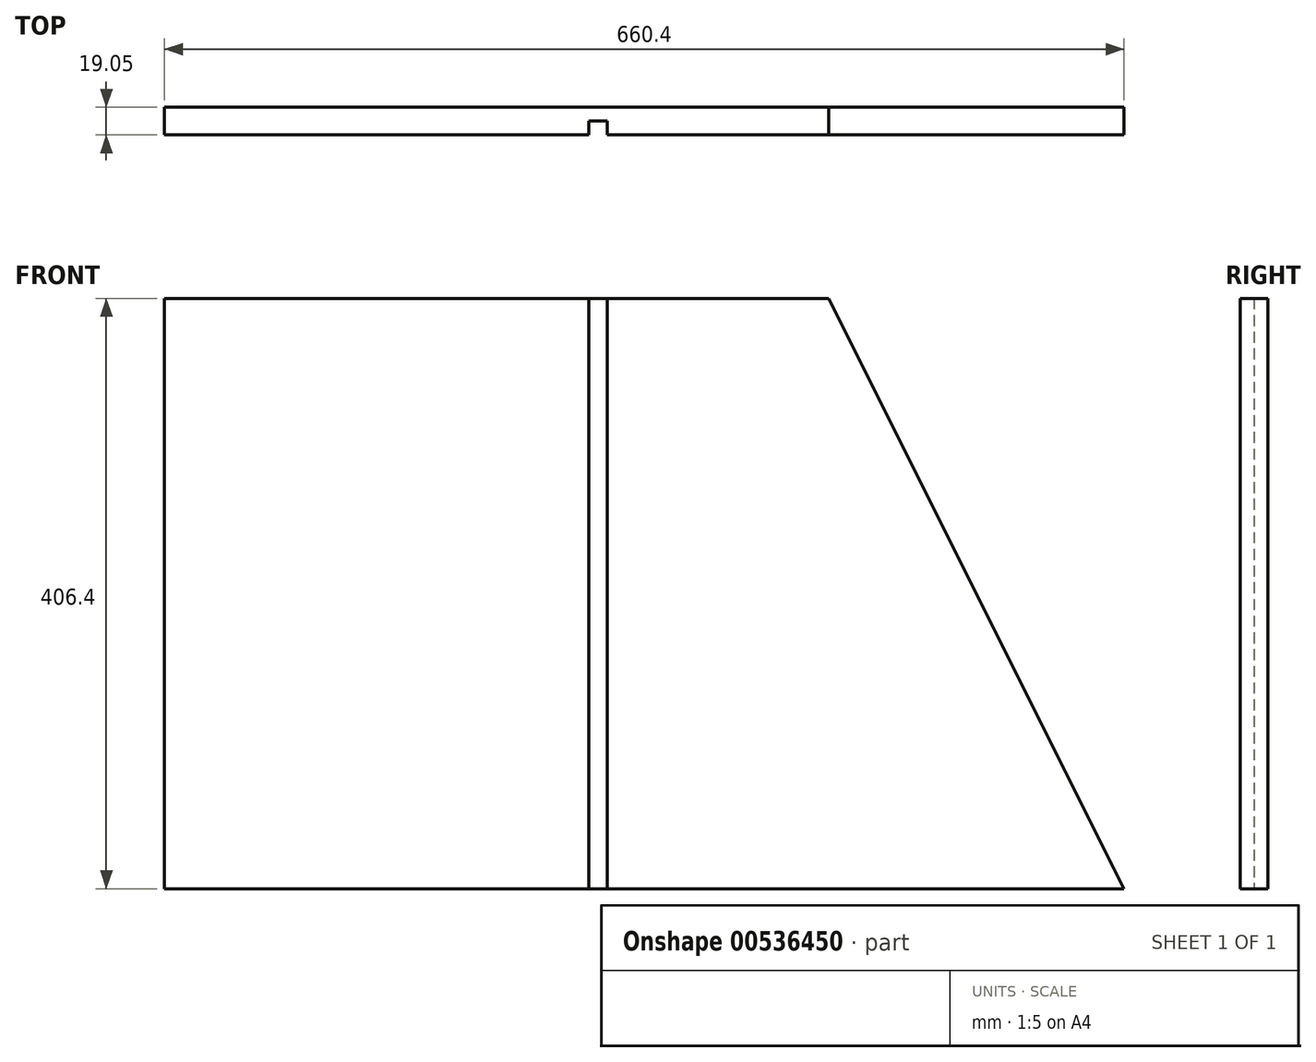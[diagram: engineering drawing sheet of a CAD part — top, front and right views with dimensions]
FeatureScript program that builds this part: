
annotation { "Feature Type Name" : "Feature", "Feature Type Description" : "" }
export const myFeature = defineFeature(function(context is Context, id is Id, definition is map)
    precondition{}
    {
        {
            var Q0;
            Q0=qCreatedBy(makeId("Front.planeOp"),FACE);
            var sketch = newSketch(context, id + "F0", { "sketchPlane" : qUnion([Q0])});
            skLineSegment(sketch, "E0", {"start": v(-356.65, 252.41) * mm, "end": v(-229.65, 252.41) * mm});
            skLineSegment(sketch, "E1", {"start": v(-229.65, 252.41) * mm, "end": v(-26.45, -153.99) * mm});
            skLineSegment(sketch, "E2", {"start": v(-26.45, -153.99) * mm, "end": v(-686.85, -153.99) * mm});
            skLineSegment(sketch, "E3", {"start": v(-229.65, 252.41) * mm, "end": v(-229.65, -153.99) * mm});
            skLineSegment(sketch, "E4.bottom", {"start": v(-356.65, 252.41) * mm, "end": v(-686.85, 252.41) * mm});
            skLineSegment(sketch, "E4.top", {"start": v(-356.65, -153.99) * mm, "end": v(-686.85, -153.99) * mm});
            skLineSegment(sketch, "E4.right", {"start": v(-686.85, 252.41) * mm, "end": v(-686.85, -153.99) * mm});
            skSolve(sketch);
        }
        {
            var Q0;
            {var subQ0=sQuery(id+"F0.wireOp",EDGE,"nFMApCBA-aBbS-xDlN-ZNX0-Un9WT2dHDHLE");Q0=makeQuery(id+"F0.imprint","IMPRINT",FACE,{"disambiguationData":[TD([[makeQuery(id+"F0.imprint","IMPRINT",EDGE,{"derivedFrom":subQ0}),-1.0]])]});}
            var Q1;
            Q1=makeQuery(id+"F0.imprint","IMPRINT",FACE,{"disambiguationData":[TD([[makeQuery(id+"F0.imprint","IMPRINT",EDGE,{"derivedFrom":sQuery(id+"F0.wireOp",EDGE,"E0")}),-1.0]])]});
            var Q2;
            {var subQ0=sQuery(id+"F0.wireOp",EDGE,"E1");Q2=makeQuery(id+"F0.imprint","IMPRINT",FACE,{"disambiguationData":[TD([[makeQuery(id+"F0.imprint","IMPRINT",EDGE,{"derivedFrom":subQ0}),-1.0]])]});}
            extrude(context, id + "F1", {"entities" : qUnion([Q0, Q1, Q2]), "depth" : 19.05 * mm, "offsetDistance" : 25.4 * mm});
        }
        {
            var Q0;
            Q0=makeQuery(id+"F1.opExtrude","CAP_FACE",FACE,{"disambiguationData":[OSD([sQuery(id+"F0.wireOp",EDGE,"E0"),sQuery(id+"F0.wireOp",EDGE,"E1"),sQuery(id+"F0.wireOp",EDGE,"E2"),sQuery(id+"F0.wireOp",EDGE,"nFMApCBA-aBbS-xDlN-ZNX0-Un9WT2dHDHLE")])],"isStart":false});
            var sketch = newSketch(context, id + "F2", { "sketchPlane" : qUnion([Q0])});
            skLineSegment(sketch, "E5", {"start": v(-229.65, 252.41) * mm, "end": v(-229.65, -153.99) * mm});
            skLineSegment(sketch, "E6.0", {"start": v(-382.05, 252.41) * mm, "end": v(-382.05, -153.99) * mm});
            skLineSegment(sketch, "E7.0", {"start": v(-394.75, 252.41) * mm, "end": v(-394.75, -153.99) * mm});
            skLineSegment(sketch, "E8.bottom", {"start": v(-394.75, 252.41) * mm, "end": v(-382.05, 252.41) * mm});
            skLineSegment(sketch, "E8.top", {"start": v(-394.75, -153.99) * mm, "end": v(-382.05, -153.99) * mm});
            skSolve(sketch);
        }
        {
            var Q0;
            Q0 = qSketchRegion(id + "F2", true);
            extrude(context, id + "F3", {"entities" : qUnion([Q0]), "operationType" : NewBodyOperationType.REMOVE, "oppositeDirection" : true, "depth" : 9.52 * mm, "offsetDistance" : 25.4 * mm});
        }
    });
